# Revit family: QF_ELECTROLUXPROFESSIONAL_589592_MCEAGBB3OO
name_source: partatom
category: Specialty Equipment
revit_build: Autodesk Revit 2018 (Build: 20190510_1515(x64)
units: mm (PartAtom-declared; Revit-internal decimal feet)

## family parameters
Always vertical = Yes
Cut with Voids When Loaded = No
Part Type = Normal
Room Calculation Point = No
Round Connector Dimension = Use Diameter
Shared = No
Work Plane-Based = No

## types (1)
- QF_ELECTROLUXPROFESSIONAL_589592_MCEAGBB3OO
    Cold Water Flow = 0 GPM
    Cold Water Maximum Pressure = 0.00 psi
    Cold Water Minimum Pressure = 0.00 psi
    Cold Water Size = 1"
    Description = WATER MIXING TAP,LEVER,1S,BS,200X900X700
    Direct Waste Size = 0"
    HP = 0 HP
    Hot Water Consumption = 0 GPM
    Hot Water Flow = 0 GPM
    Hot Water Maximum Pressure = 0.00 psi
    Hot Water Minimum Pressure = 0.00 psi
    Hot Water Size = 1"
    Manufacturer = ELECTROLUX
    Model = 589592
    URL = www.electrolux.com/professional
    URL Cutsheet = www.electrolux.com/professional
    Watts = 0 W
    Weight in Pounds = 61.72

## geometry (parser evidence)
native form markers: Blend x4, Sweep x6
no freeform markers — native parametric forms only
